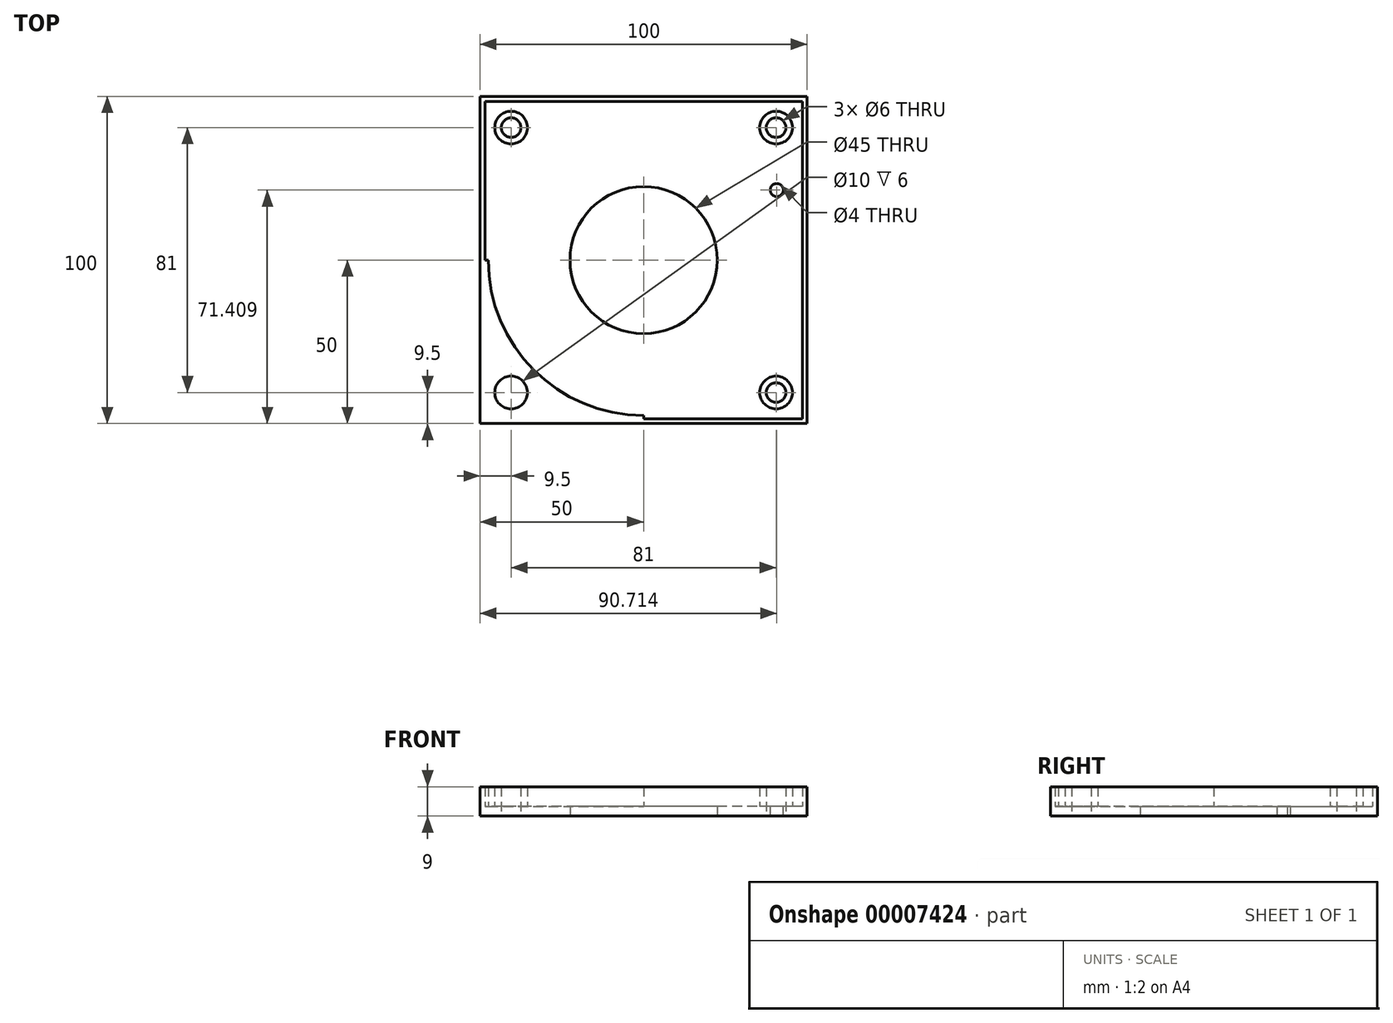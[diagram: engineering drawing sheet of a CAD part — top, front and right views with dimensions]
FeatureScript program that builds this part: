
annotation { "Feature Type Name" : "Feature", "Feature Type Description" : "" }
export const myFeature = defineFeature(function(context is Context, id is Id, definition is map)
    precondition{}
    {
        {
            var Q0;
            Q0=qCreatedBy(makeId("Top.planeOp"),FACE);
            var sketch = newSketch(context, id + "F0", { "sketchPlane" : qUnion([Q0])});
            skLineSegment(sketch, "E0.rect.bottom", {"start": v(50, 50) * mm, "end": v(-50, 50) * mm});
            skLineSegment(sketch, "E0.rect.top", {"start": v(50, -50) * mm, "end": v(-50, -50) * mm});
            skLineSegment(sketch, "E0.rect.left", {"start": v(50, 50) * mm, "end": v(50, -50) * mm});
            skLineSegment(sketch, "E0.rect.right", {"start": v(-50, 50) * mm, "end": v(-50, -50) * mm});
            skPoint(sketch, "E0.rect.middle", {"position": v(0, 0) * mm});
            skCircle(sketch, "E1", {"center": v(0, 0) * mm, "radius": 22.5 * mm});
            skSolve(sketch);
        }
        {
            var Q0;
            Q0=makeQuery(id+"F0.imprint","IMPRINT",FACE,{"disambiguationData":[TD([[makeQuery(id+"F0.imprint","IMPRINT",EDGE,{"derivedFrom":sQuery(id+"F0.wireOp",EDGE,"E0.rect.bottom")}),1.0]])]});
            extrude(context, id + "F1", {"entities" : qUnion([Q0]), "depth" : 3 * mm});
        }
        {
            var Q0;
            Q0=makeQuery(id+"F1.opExtrude","CAP_FACE",FACE,{"disambiguationData":[OSD([sQuery(id+"F0.wireOp",EDGE,"E0.rect.bottom"),sQuery(id+"F0.wireOp",EDGE,"E0.rect.top"),sQuery(id+"F0.wireOp",EDGE,"E0.rect.left"),sQuery(id+"F0.wireOp",EDGE,"E0.rect.right")])],"isStart":false});
            var sketch = newSketch(context, id + "F2", { "sketchPlane" : qUnion([Q0])});
            skLineSegment(sketch, "E2.rect.bottom", {"start": v(48.5, -48.5) * mm, "end": v(-48.5, -48.5) * mm});
            skLineSegment(sketch, "E2.rect.top", {"start": v(48.5, 48.5) * mm, "end": v(-48.5, 48.5) * mm});
            skLineSegment(sketch, "E2.rect.left", {"start": v(48.5, -48.5) * mm, "end": v(48.5, 48.5) * mm});
            skLineSegment(sketch, "E2.rect.right", {"start": v(-48.5, -48.5) * mm, "end": v(-48.5, 48.5) * mm});
            skPoint(sketch, "E2.rect.middle", {"position": v(0, 0) * mm});
            skSolve(sketch);
        }
        {
            var Q0;
            Q0=makeQuery(id+"F2.imprint","IMPRINT",FACE,{"disambiguationData":[TD([[makeQuery(id+"F2.imprint","IMPRINT",EDGE,{"derivedFrom":sQuery(id+"F2.wireOp",EDGE,"E2.rect.bottom")}),1.0]])]});
            extrude(context, id + "F3", {"entities" : qUnion([Q0]), "operationType" : NewBodyOperationType.ADD, "depth" : 6 * mm});
        }
        {
            var Q0;
            Q0=makeQuery(id+"F1.opExtrude","CAP_FACE",FACE,{"disambiguationData":[OSD([sQuery(id+"F0.wireOp",EDGE,"E0.rect.bottom"),sQuery(id+"F0.wireOp",EDGE,"E0.rect.top"),sQuery(id+"F0.wireOp",EDGE,"E0.rect.left"),sQuery(id+"F0.wireOp",EDGE,"E0.rect.right"),sQuery(id+"F0.wireOp",EDGE,"E1")])],"isStart":false});
            var sketch = newSketch(context, id + "F4", { "sketchPlane" : qUnion([Q0])});
            skCircle(sketch, "E3", {"center": v(0, 0) * mm, "radius": 47.5 * mm});
            skLineSegment(sketch, "E4", {"start": v(-48.5, 40.5) * mm, "end": v(48.5, 40.5) * mm});
            skLineSegment(sketch, "E5", {"start": v(-40.5, 48.5) * mm, "end": v(-40.5, 40.5) * mm});
            skLineSegment(sketch, "E6", {"start": v(40.5, 48.5) * mm, "end": v(40.5, 40.5) * mm});
            skLineSegment(sketch, "E7", {"start": v(40.5, 44.5) * mm, "end": v(48.5, 44.5) * mm});
            skLineSegment(sketch, "E8", {"start": v(-48.5, 43.88) * mm, "end": v(-40.5, 43.88) * mm});
            skCircle(sketch, "E9", {"center": v(-40.5, 40.5) * mm, "radius": 5 * mm});
            skCircle(sketch, "E10", {"center": v(-40.5, 40.5) * mm, "radius": 3 * mm});
            skLineSegment(sketch, "E11", {"start": v(-48.5, 0) * mm, "end": v(48.5, 0) * mm});
            skLineSegment(sketch, "E12", {"start": v(0, 48.5) * mm, "end": v(0, -48.5) * mm});
            skCircle(sketch, "E13.0.MirrorC", {"center": v(40.5, 40.5) * mm, "radius": 5 * mm});
            skCircle(sketch, "E14.0.MirrorC", {"center": v(40.5, 40.5) * mm, "radius": 3 * mm});
            skCircle(sketch, "E15.0.MirrorC", {"center": v(-40.5, -40.5) * mm, "radius": 5 * mm});
            skCircle(sketch, "E16.0.MirrorC", {"center": v(-40.5, -40.5) * mm, "radius": 3 * mm});
            skCircle(sketch, "E17.0.MirrorC", {"center": v(40.5, -40.5) * mm, "radius": 3 * mm});
            skCircle(sketch, "E18.0.MirrorC", {"center": v(40.5, -40.5) * mm, "radius": 5 * mm});
            skSolve(sketch);
        }
        {
            var Q0;
            Q0=makeQuery(id+"F4.imprint","IMPRINT",FACE,{"disambiguationData":[TD([[makeQuery(id+"F4.imprint","IMPRINT",EDGE,{"derivedFrom":sQuery(id+"F4.wireOp",EDGE,"E15.0.MirrorC")}),-1.0]])]});
            var Q1;
            {var subQ3=sQuery(id+"F4.wireOp",EDGE,"E4");var subQ5=sQuery(id+"F4.wireOp",EDGE,"E10");var subQ7=makeQuery(id+"F4.imprint","INTERSECT",VERTEX,{"disambiguationData":[OD(1.0)],"derivedFrom":[subQ3,subQ5]});Q1=makeQuery(id+"F4.imprint","IMPRINT",FACE,{"disambiguationData":[TD([[makeQuery(id+"F4.imprint","IMPRINT",EDGE,{"disambiguationData":[TD([[subQ7,-1.0]])],"derivedFrom":subQ3}),1.0]])]});}
            var Q2;
            {var subQ1=sQuery(id+"F4.wireOp",EDGE,"E4");var subQ4=sQuery(id+"F4.wireOp",EDGE,"E9");var subQ6=makeQuery(id+"F4.imprint","INTERSECT",VERTEX,{"disambiguationData":[OD(0.0)],"derivedFrom":[subQ1,subQ4]});Q2=makeQuery(id+"F4.imprint","IMPRINT",FACE,{"disambiguationData":[TD([[makeQuery(id+"F4.imprint","IMPRINT",EDGE,{"disambiguationData":[TD([[subQ6,-1.0]])],"derivedFrom":subQ1}),-1.0]])]});}
            var Q3;
            {var subQ3=sQuery(id+"F4.wireOp",EDGE,"E4");var subQ5=sQuery(id+"F4.wireOp",EDGE,"E9");var subQ8=makeQuery(id+"F4.imprint","INTERSECT",VERTEX,{"disambiguationData":[OD(0.0)],"derivedFrom":[subQ3,subQ5]});Q3=makeQuery(id+"F4.imprint","IMPRINT",FACE,{"disambiguationData":[TD([[makeQuery(id+"F4.imprint","IMPRINT",EDGE,{"disambiguationData":[TD([[subQ8,-1.0]])],"derivedFrom":subQ3}),1.0]])]});}
            var Q4;
            {var subQ1=sQuery(id+"F4.wireOp",EDGE,"E8");var subQ3=sQuery(id+"F4.wireOp",EDGE,"E5");var subQ5=makeQuery(id+"F4.imprint","INTERSECT",VERTEX,{"derivedFrom":[subQ3,subQ1]});Q4=makeQuery(id+"F4.imprint","IMPRINT",FACE,{"disambiguationData":[TD([[makeQuery(id+"F4.imprint","IMPRINT",EDGE,{"disambiguationData":[TD([[subQ5,1.0]])],"derivedFrom":subQ3}),-1.0]])]});}
            var Q5;
            {var subQ1=sQuery(id+"F4.wireOp",EDGE,"E7");var subQ3=sQuery(id+"F4.wireOp",EDGE,"E6");var subQ5=makeQuery(id+"F4.imprint","INTERSECT",VERTEX,{"derivedFrom":[subQ3,subQ1]});Q5=makeQuery(id+"F4.imprint","IMPRINT",FACE,{"disambiguationData":[TD([[makeQuery(id+"F4.imprint","IMPRINT",EDGE,{"disambiguationData":[TD([[subQ5,1.0]])],"derivedFrom":subQ3}),1.0]])]});}
            var Q6;
            {var subQ3=sQuery(id+"F4.wireOp",EDGE,"E4");var subQ5=sQuery(id+"F4.wireOp",EDGE,"E14.0.MirrorC");var subQ8=makeQuery(id+"F4.imprint","INTERSECT",VERTEX,{"disambiguationData":[OD(1.0)],"derivedFrom":[subQ3,subQ5]});Q6=makeQuery(id+"F4.imprint","IMPRINT",FACE,{"disambiguationData":[TD([[makeQuery(id+"F4.imprint","IMPRINT",EDGE,{"disambiguationData":[TD([[subQ8,-1.0]])],"derivedFrom":subQ3}),1.0]])]});}
            var Q7;
            {var subQ3=sQuery(id+"F4.wireOp",EDGE,"E4");var subQ6=sQuery(id+"F4.wireOp",EDGE,"E13.0.MirrorC");var subQ8=makeQuery(id+"F4.imprint","INTERSECT",VERTEX,{"disambiguationData":[OD(0.0)],"derivedFrom":[subQ3,subQ6]});Q7=makeQuery(id+"F4.imprint","IMPRINT",FACE,{"disambiguationData":[TD([[makeQuery(id+"F4.imprint","IMPRINT",EDGE,{"disambiguationData":[TD([[subQ8,-1.0]])],"derivedFrom":subQ3}),1.0]])]});}
            var Q8;
            {var subQ1=sQuery(id+"F4.wireOp",EDGE,"E4");var subQ4=sQuery(id+"F4.wireOp",EDGE,"E13.0.MirrorC");var subQ6=makeQuery(id+"F4.imprint","INTERSECT",VERTEX,{"disambiguationData":[OD(0.0)],"derivedFrom":[subQ1,subQ4]});Q8=makeQuery(id+"F4.imprint","IMPRINT",FACE,{"disambiguationData":[TD([[makeQuery(id+"F4.imprint","IMPRINT",EDGE,{"disambiguationData":[TD([[subQ6,-1.0]])],"derivedFrom":subQ1}),-1.0]])]});}
            var Q9;
            Q9=makeQuery(id+"F4.imprint","IMPRINT",FACE,{"disambiguationData":[TD([[makeQuery(id+"F4.imprint","IMPRINT",EDGE,{"derivedFrom":sQuery(id+"F4.wireOp",EDGE,"E17.0.MirrorC")}),-1.0]])]});
            var Q10;
            Q10=sQuery(id+"F4.wireOp",EDGE,"E16.0.MirrorC");
            var Q11;
            Q11=sQuery(id+"F4.wireOp",EDGE,"E15.0.MirrorC");
            extrude(context, id + "F5", {"entities" : qUnion([Q0, Q1, Q2, Q3, Q4, Q5, Q6, Q7, Q8, Q9]), "operationType" : NewBodyOperationType.ADD, "surfaceEntities" : qUnion([Q10, Q11]), "depth" : 6 * mm});
        }
        {
            var Q0;
            Q0=makeQuery(id+"F5.boolean.opBoolean","SPLIT",FACE,{"disambiguationData":[TD([makeQuery(id+"F5.opExtrude","SWEPT_FACE",FACE,{"disambiguationData":[OSD([sQuery(id+"F4.wireOp",EDGE,"E10")])]})])],"derivedFrom":makeQuery(id+"F1.opExtrude","CAP_FACE",FACE,{"disambiguationData":[OSD([sQuery(id+"F0.wireOp",EDGE,"E0.rect.bottom"),sQuery(id+"F0.wireOp",EDGE,"E0.rect.top"),sQuery(id+"F0.wireOp",EDGE,"E0.rect.left"),sQuery(id+"F0.wireOp",EDGE,"E0.rect.right"),sQuery(id+"F0.wireOp",EDGE,"E1")])],"isStart":false})});
            var Q1;
            Q1=makeQuery(id+"F5.boolean.opBoolean","SPLIT",FACE,{"disambiguationData":[TD([makeQuery(id+"F5.opExtrude","SWEPT_FACE",FACE,{"disambiguationData":[OSD([sQuery(id+"F4.wireOp",EDGE,"E14.0.MirrorC")])]})])],"derivedFrom":makeQuery(id+"F1.opExtrude","CAP_FACE",FACE,{"disambiguationData":[OSD([sQuery(id+"F0.wireOp",EDGE,"E0.rect.bottom"),sQuery(id+"F0.wireOp",EDGE,"E0.rect.top"),sQuery(id+"F0.wireOp",EDGE,"E0.rect.left"),sQuery(id+"F0.wireOp",EDGE,"E0.rect.right"),sQuery(id+"F0.wireOp",EDGE,"E1")])],"isStart":false})});
            var Q2;
            Q2=makeQuery(id+"F5.boolean.opBoolean","SPLIT",FACE,{"disambiguationData":[TD([makeQuery(id+"F5.opExtrude","SWEPT_FACE",FACE,{"disambiguationData":[OSD([sQuery(id+"F4.wireOp",EDGE,"E17.0.MirrorC")])]})])],"derivedFrom":makeQuery(id+"F1.opExtrude","CAP_FACE",FACE,{"disambiguationData":[OSD([sQuery(id+"F0.wireOp",EDGE,"E0.rect.bottom"),sQuery(id+"F0.wireOp",EDGE,"E0.rect.top"),sQuery(id+"F0.wireOp",EDGE,"E0.rect.left"),sQuery(id+"F0.wireOp",EDGE,"E0.rect.right"),sQuery(id+"F0.wireOp",EDGE,"E1")])],"isStart":false})});
            var Q3;
            Q3=makeQuery(id+"F5.boolean.opBoolean","SPLIT",FACE,{"disambiguationData":[TD([makeQuery(id+"F5.opExtrude","SWEPT_FACE",FACE,{"disambiguationData":[OSD([sQuery(id+"F4.wireOp",EDGE,"E16.0.MirrorC")])]})])],"derivedFrom":makeQuery(id+"F1.opExtrude","CAP_FACE",FACE,{"disambiguationData":[OSD([sQuery(id+"F0.wireOp",EDGE,"E0.rect.bottom"),sQuery(id+"F0.wireOp",EDGE,"E0.rect.top"),sQuery(id+"F0.wireOp",EDGE,"E0.rect.left"),sQuery(id+"F0.wireOp",EDGE,"E0.rect.right"),sQuery(id+"F0.wireOp",EDGE,"E1")])],"isStart":false})});
            extrude(context, id + "F6", {"entities" : qUnion([Q0, Q1, Q2, Q3]), "operationType" : NewBodyOperationType.REMOVE, "endBound" : BoundingType.THROUGH_ALL, "oppositeDirection" : true, "depth" : 25 * mm});
        }
        {
            var Q0;
            {var subQ0=sQuery(id+"F0.wireOp",EDGE,"E1");Q0=makeQuery(id+"F5.boolean.opBoolean","SPLIT",FACE,{"disambiguationData":[TD([makeQuery(id+"F1.opExtrude","SWEPT_FACE",FACE,{"disambiguationData":[OSD([subQ0])]})])],"derivedFrom":makeQuery(id+"F1.opExtrude","CAP_FACE",FACE,{"disambiguationData":[OSD([sQuery(id+"F0.wireOp",EDGE,"E0.rect.bottom"),sQuery(id+"F0.wireOp",EDGE,"E0.rect.top"),sQuery(id+"F0.wireOp",EDGE,"E0.rect.left"),sQuery(id+"F0.wireOp",EDGE,"E0.rect.right"),subQ0])],"isStart":false})});}
            var sketch = newSketch(context, id + "F7", { "sketchPlane" : qUnion([Q0])});
            skCircle(sketch, "E19", {"center": v(0, 0) * mm, "radius": 46 * mm, "construction": true});
            skPoint(sketch, "E20", {"position": v(40.71, 21.4) * mm});
            skCircle(sketch, "E21", {"center": v(40.71, 21.4) * mm, "radius": 2 * mm});
            skSolve(sketch);
        }
        {
            var Q0;
            Q0=makeQuery(id+"F7.imprint","IMPRINT",FACE,{"disambiguationData":[TD([[makeQuery(id+"F7.imprint","IMPRINT",EDGE,{"derivedFrom":sQuery(id+"F7.wireOp",EDGE,"E21")}),1.0]])]});
            extrude(context, id + "F8", {"entities" : qUnion([Q0]), "operationType" : NewBodyOperationType.REMOVE, "oppositeDirection" : true, "depth" : 25 * mm});
        }
    });
